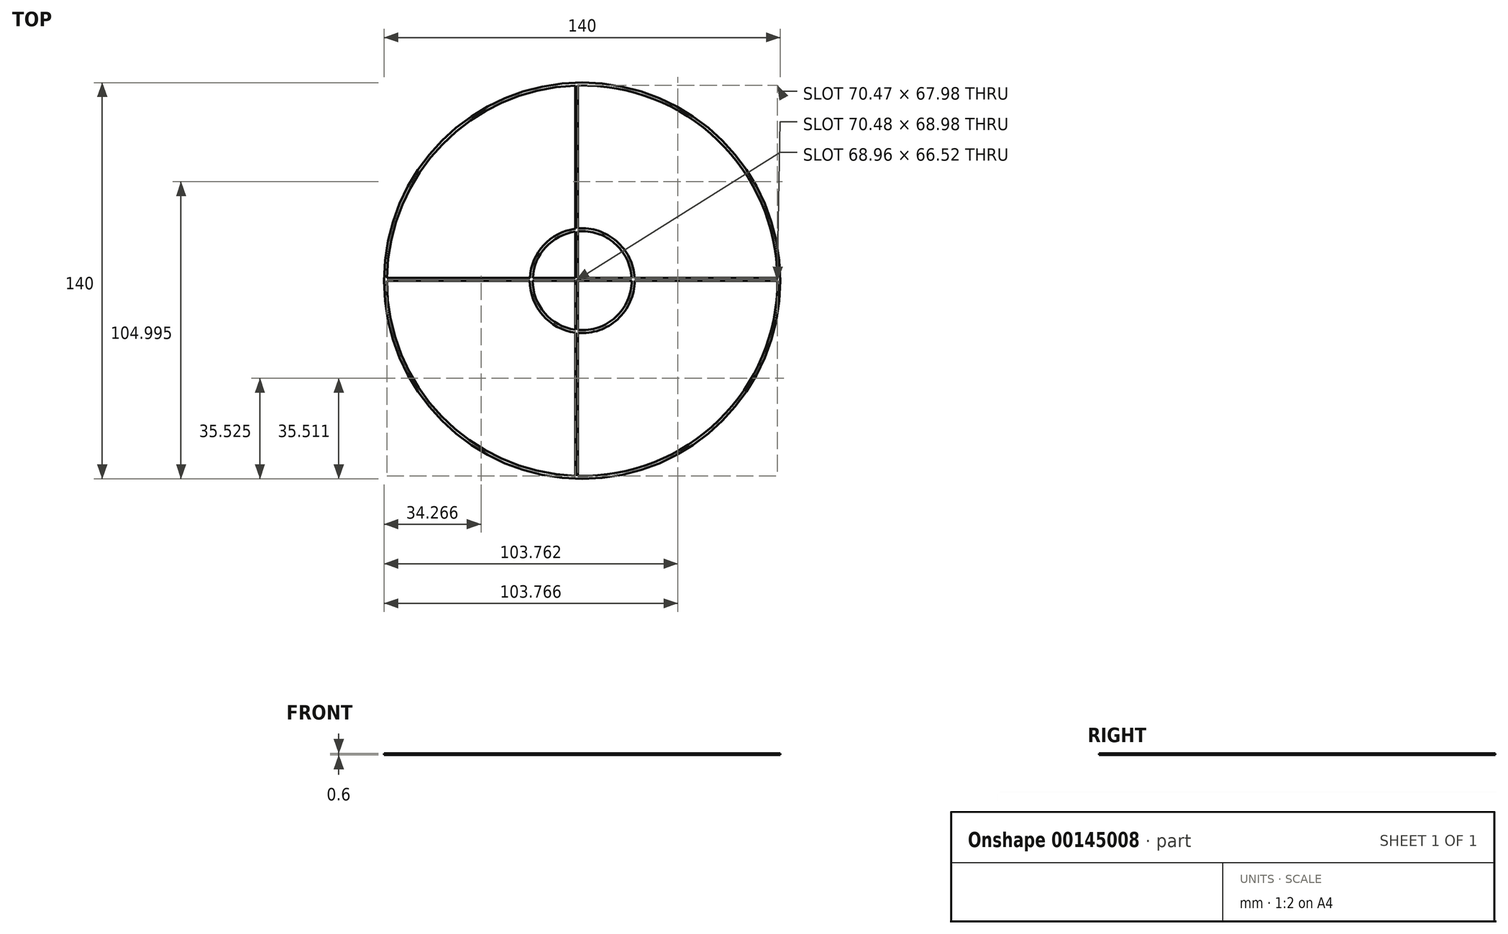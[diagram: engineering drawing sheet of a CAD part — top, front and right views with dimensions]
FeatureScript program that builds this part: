
annotation { "Feature Type Name" : "Feature", "Feature Type Description" : "" }
export const myFeature = defineFeature(function(context is Context, id is Id, definition is map)
    precondition{}
    {
        {
            var Q0;
            Q0=qCreatedBy(makeId("Top.planeOp"),FACE);
            var sketch = newSketch(context, id + "F0", { "sketchPlane" : qUnion([Q0])});
            skCircle(sketch, "E0", {"center": v(0.12, -0.5) * mm, "radius": 70 * mm});
            skArc(sketch, "E1", {"start": v(-2.35, 68.46) * mm, "mid": v(-49.19, 47.77) * mm, "end": v(-68.87, 0.5) * mm});
            skLineSegment(sketch, "E2", {"start": v(-2.35, 68.46) * mm, "end": v(-2.35, 17.84) * mm});
            skLineSegment(sketch, "E3", {"start": v(-1.35, -69.48) * mm, "end": v(-1.35, -18.94) * mm});
            skArc(sketch, "E4.trimOffspring", {"start": v(-1.35, -69.48) * mm, "mid": v(48.39, -49.8) * mm, "end": v(69.12, -0.5) * mm});
            skLineSegment(sketch, "E5", {"start": v(69.12, 0.5) * mm, "end": v(18.6, 0.5) * mm});
            skLineSegment(sketch, "E6", {"start": v(-68.88, -0.5) * mm, "end": v(-18.38, -0.5) * mm});
            skArc(sketch, "E7", {"start": v(-17.38, -0.5) * mm, "mid": v(-13.1, -11.96) * mm, "end": v(-2.35, -17.82) * mm});
            skArc(sketch, "E8", {"start": v(-18.38, -0.5) * mm, "mid": v(-13.8, -12.67) * mm, "end": v(-2.35, -18.83) * mm});
            skArc(sketch, "E9.trimOffspring", {"start": v(-68.88, -0.5) * mm, "mid": v(-49.53, -48.4) * mm, "end": v(-2.35, -69.45) * mm});
            skLineSegment(sketch, "E10.trimOffspring", {"start": v(-18.35, 0.5) * mm, "end": v(-68.87, 0.5) * mm});
            skLineSegment(sketch, "E11.trimOffspring", {"start": v(-17.38, -0.5) * mm, "end": v(-2.35, -0.5) * mm});
            skLineSegment(sketch, "E12.trimOffspring", {"start": v(-2.35, -0.5) * mm, "end": v(-2.35, -17.82) * mm});
            skLineSegment(sketch, "E13.trimOffspring", {"start": v(-1.35, 0.5) * mm, "end": v(-1.35, 16.94) * mm});
            skLineSegment(sketch, "E14.trimOffspring", {"start": v(-2.35, 0.5) * mm, "end": v(-17.35, 0.5) * mm});
            skLineSegment(sketch, "E15.trimOffspring", {"start": v(-1.35, -0.5) * mm, "end": v(17.62, -0.5) * mm});
            skArc(sketch, "E16.trimOffspring", {"start": v(-1.35, -18.94) * mm, "mid": v(12.67, -14.1) * mm, "end": v(18.62, -0.5) * mm});
            skArc(sketch, "E17.trimOffspring", {"start": v(-1.35, -17.93) * mm, "mid": v(11.96, -13.38) * mm, "end": v(17.62, -0.5) * mm});
            skLineSegment(sketch, "E18.trimOffspring", {"start": v(-2.35, -18.83) * mm, "end": v(-2.35, -69.45) * mm});
            skLineSegment(sketch, "E19.trimOffspring", {"start": v(-1.35, -17.93) * mm, "end": v(-1.35, -0.5) * mm});
            skLineSegment(sketch, "E20.trimOffspring", {"start": v(-1.35, 17.94) * mm, "end": v(-1.35, 68.49) * mm});
            skArc(sketch, "E21.trimOffspring", {"start": v(-2.35, 17.84) * mm, "mid": v(-13.47, 12.05) * mm, "end": v(-18.35, 0.5) * mm});
            skLineSegment(sketch, "E22.trimOffspring", {"start": v(-2.35, 16.83) * mm, "end": v(-2.35, 0.5) * mm});
            skArc(sketch, "E23.trimOffspring", {"start": v(-2.35, 16.83) * mm, "mid": v(-12.76, 11.34) * mm, "end": v(-17.35, 0.5) * mm});
            skLineSegment(sketch, "E24.trimOffspring", {"start": v(17.6, 0.5) * mm, "end": v(-1.35, 0.5) * mm});
            skArc(sketch, "E25.trimOffspring", {"start": v(18.6, 0.5) * mm, "mid": v(12.3, 13.43) * mm, "end": v(-1.35, 17.94) * mm});
            skArc(sketch, "E26.trimOffspring", {"start": v(17.6, 0.5) * mm, "mid": v(11.6, 12.72) * mm, "end": v(-1.35, 16.94) * mm});
            skLineSegment(sketch, "E27.trimOffspring", {"start": v(18.62, -0.5) * mm, "end": v(69.12, -0.5) * mm});
            skArc(sketch, "E28.trimOffspring", {"start": v(69.12, 0.5) * mm, "mid": v(48.03, 49.16) * mm, "end": v(-1.35, 68.49) * mm});
            skSolve(sketch);
        }
        {
            var Q0;
            Q0=makeQuery(id+"F0.imprint","IMPRINT",FACE,{"disambiguationData":[TD([[makeQuery(id+"F0.imprint","IMPRINT",EDGE,{"derivedFrom":sQuery(id+"F0.wireOp",EDGE,"E0")}),1.0]])]});
            extrude(context, id + "F1", {"entities" : qUnion([Q0]), "depth" : 0.6 * mm});
        }
    });
